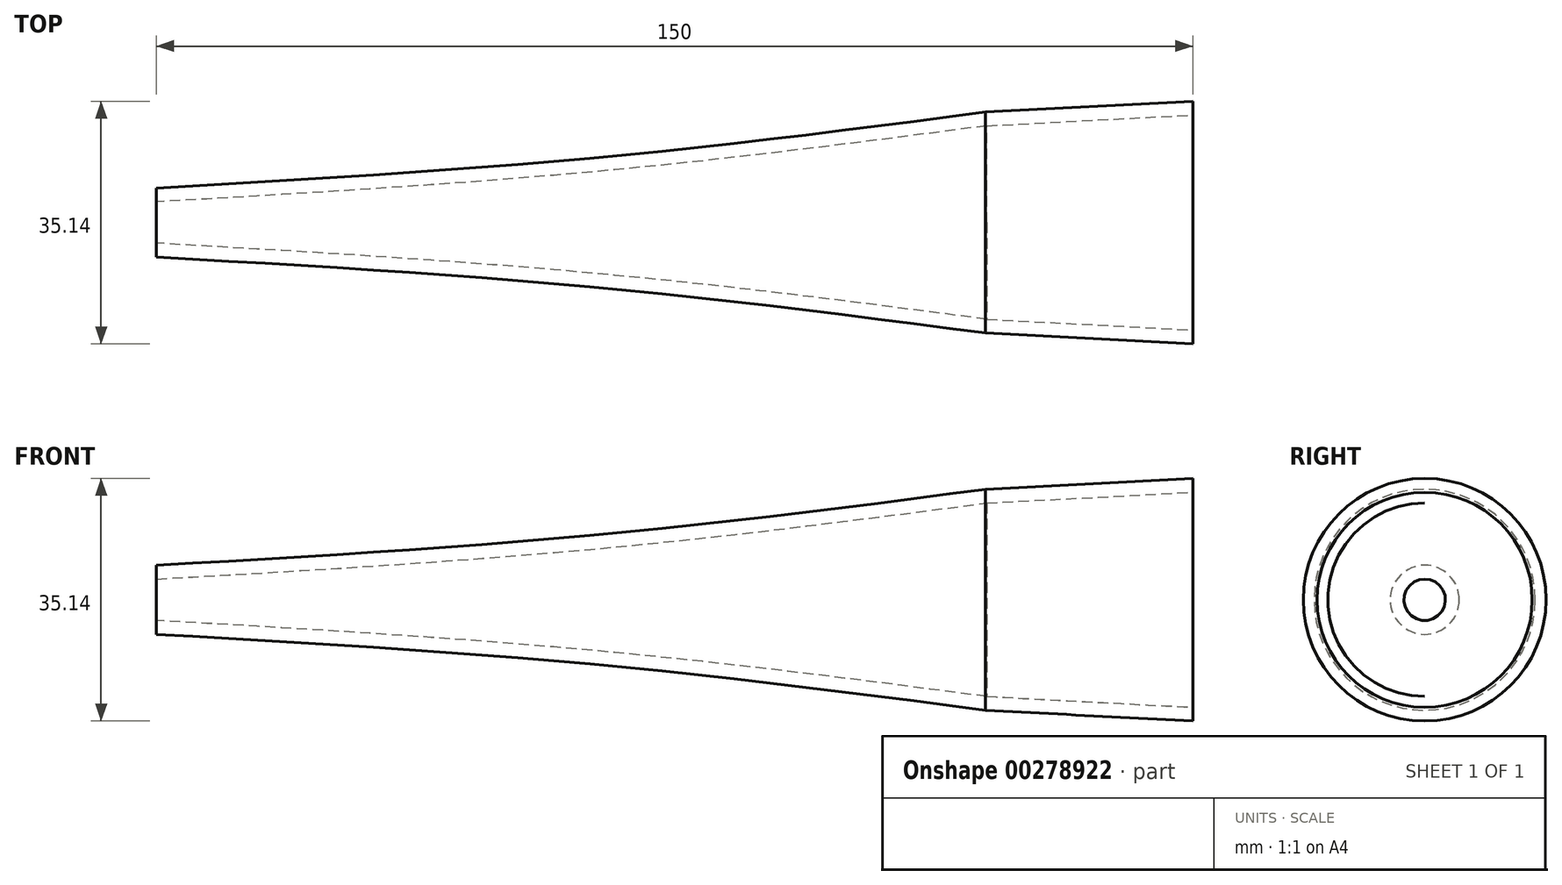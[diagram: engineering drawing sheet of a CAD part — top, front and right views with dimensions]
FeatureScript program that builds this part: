
annotation { "Feature Type Name" : "Feature", "Feature Type Description" : "" }
export const myFeature = defineFeature(function(context is Context, id is Id, definition is map)
    precondition{}
    {
        {
            var Q0;
            Q0=qCreatedBy(makeId("Right.planeOp"),FACE);
            cPlane(context, id + "F0", {"entities" : qUnion([Q0]), "cplaneType" : CPlaneType.OFFSET, "offset" : 70 * mm, "width" : 152.4 * mm, "height" : 152.4 * mm});
        }
        {
            var Q0;
            Q0=qCreatedBy(id+"F0.planeOp",FACE);
            cPlane(context, id + "F1", {"entities" : qUnion([Q0]), "cplaneType" : CPlaneType.OFFSET, "offset" : 50 * mm, "width" : 150 * mm, "height" : 150 * mm});
        }
        {
            var Q0;
            Q0=qCreatedBy(id+"F0.planeOp",FACE);
            var sketch = newSketch(context, id + "F2", { "sketchPlane" : qUnion([Q0])});
            skCircle(sketch, "E0", {"center": v(0, 0) * mm, "radius": 10 * mm});
            skSolve(sketch);
        }
        {
            var Q0;
            Q0=qCreatedBy(id+"F1.planeOp",FACE);
            var sketch = newSketch(context, id + "F3", { "sketchPlane" : qUnion([Q0])});
            skCircle(sketch, "E1", {"center": v(0, 0) * mm, "radius": 16 * mm});
            skSolve(sketch);
        }
        {
            var Q0;
            Q0=qCreatedBy(makeId("Right.planeOp"),FACE);
            var sketch = newSketch(context, id + "F4", { "sketchPlane" : qUnion([Q0])});
            skCircle(sketch, "E2", {"center": v(0, 0) * mm, "radius": 5 * mm});
            skSolve(sketch);
        }
        {
            var Q0;
            Q0=makeQuery(id+"F4.imprint","IMPRINT",FACE,{"disambiguationData":[TD([[makeQuery(id+"F4.imprint","IMPRINT",EDGE,{"derivedFrom":sQuery(id+"F4.wireOp",EDGE,"E2")}),1.0]])]});
            var Q1;
            Q1=makeQuery(id+"F2.imprint","IMPRINT",FACE,{"disambiguationData":[TD([[makeQuery(id+"F2.imprint","IMPRINT",EDGE,{"derivedFrom":sQuery(id+"F2.wireOp",EDGE,"E0")}),1.0]])]});
            var Q2;
            Q2=makeQuery(id+"F3.imprint","IMPRINT",FACE,{"disambiguationData":[TD([[makeQuery(id+"F3.imprint","IMPRINT",EDGE,{"derivedFrom":sQuery(id+"F3.wireOp",EDGE,"E1")}),1.0]])]});
            loft(context, id + "F5", {"sheetProfilesArray" : [{ "sheetProfileEntities" : qUnion([Q0]) }, { "sheetProfileEntities" : qUnion([Q1]) }, { "sheetProfileEntities" : qUnion([Q2]) }]});
        }
        {
            var Q0;
            Q0=makeQuery(id+"F3.imprint","IMPRINT",FACE,{"disambiguationData":[TD([[makeQuery(id+"F3.imprint","IMPRINT",EDGE,{"derivedFrom":sQuery(id+"F3.wireOp",EDGE,"E1")}),1.0]])]});
            extrude(context, id + "F6", {"entities" : qUnion([Q0]), "operationType" : NewBodyOperationType.ADD, "depth" : 30 * mm, "hasDraft" : true, "draftAngle" : 3 * degree});
        }
        {
            var Q0;
            Q0=makeQuery(id+"F6.opExtrude","CAP_FACE",FACE,{"disambiguationData":[OSD([sQuery(id+"F3.wireOp",EDGE,"E1")])],"isStart":false});
            var Q1;
            Q1=makeQuery(id+"F5.opLoft","CAP_FACE",FACE,{"disambiguationData":[OSD([makeQuery(id+"F4.imprint","IMPRINT",FACE,{"disambiguationData":[TD([[makeQuery(id+"F4.imprint","IMPRINT",EDGE,{"derivedFrom":sQuery(id+"F4.wireOp",EDGE,"E2")}),1.0]])]})])],"isStart":true});
            shell(context, id + "F7", {"entities" : qUnion([Q0, Q1]), "thickness" : 2 * mm});
        }
    });
